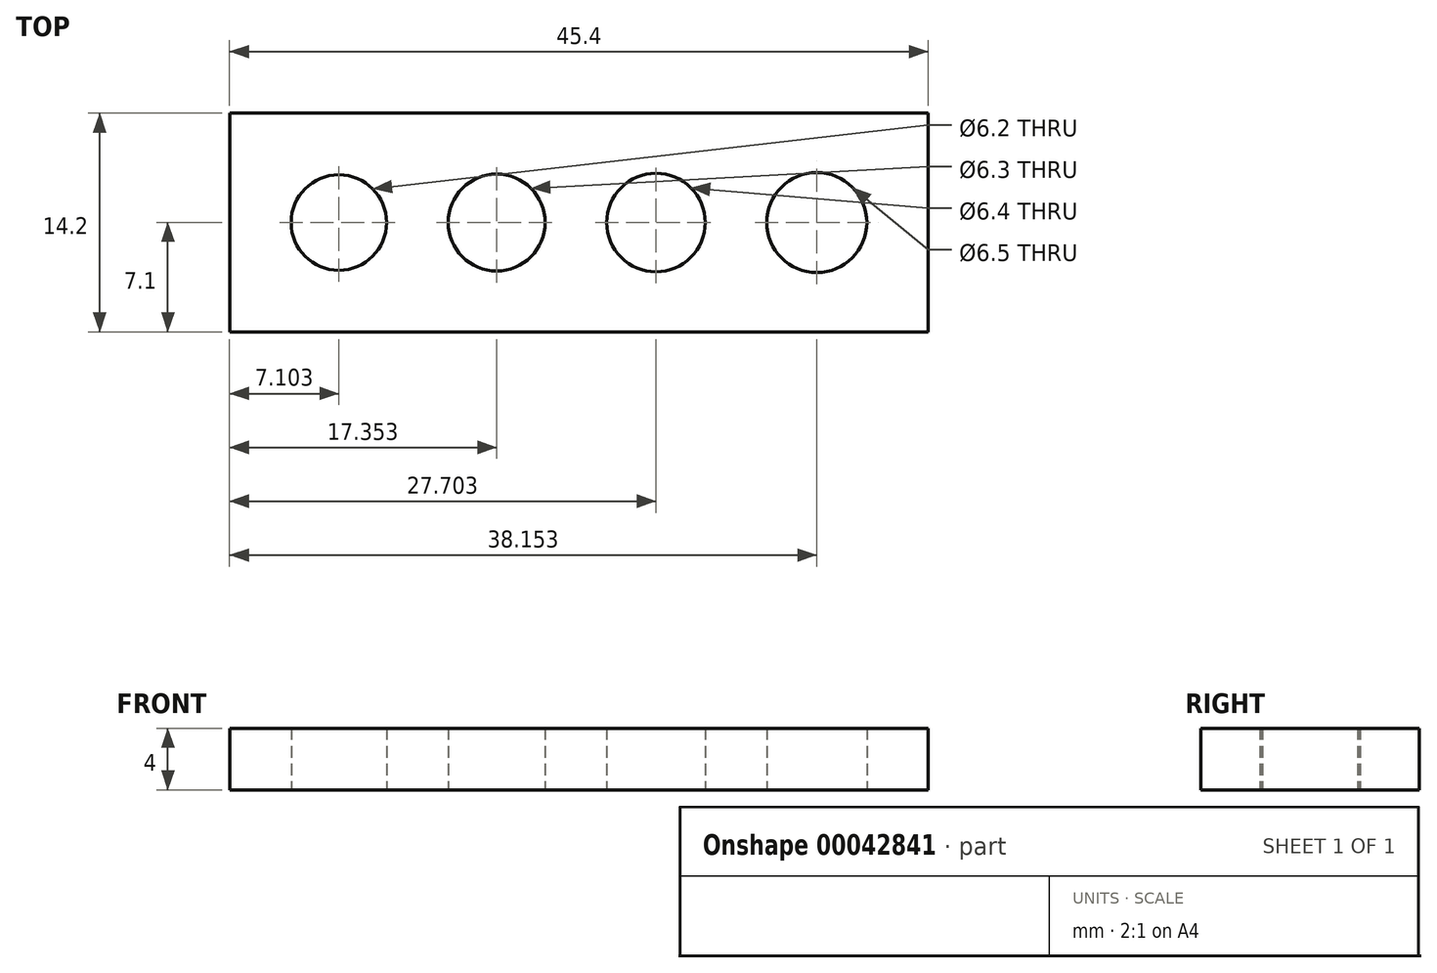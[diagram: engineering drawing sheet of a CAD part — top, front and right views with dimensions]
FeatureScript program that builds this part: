
annotation { "Feature Type Name" : "Feature", "Feature Type Description" : "" }
export const myFeature = defineFeature(function(context is Context, id is Id, definition is map)
    precondition{}
    {
        {
            var Q0;
            Q0=qCreatedBy(makeId("Top.planeOp"),FACE);
            var sketch = newSketch(context, id + "F0", { "sketchPlane" : qUnion([Q0])});
            skCircle(sketch, "E0", {"center": v(-16.23, 0) * mm, "radius": 3.1 * mm});
            skCircle(sketch, "E1", {"center": v(-5.98, 0) * mm, "radius": 3.15 * mm});
            skCircle(sketch, "E2", {"center": v(4.37, 0) * mm, "radius": 3.2 * mm});
            skCircle(sketch, "E3", {"center": v(14.82, 0) * mm, "radius": 3.25 * mm});
            skLineSegment(sketch, "E4.bottom", {"start": v(-23.33, 7.1) * mm, "end": v(22.07, 7.1) * mm});
            skLineSegment(sketch, "E4.top", {"start": v(-23.33, -7.1) * mm, "end": v(22.07, -7.1) * mm});
            skLineSegment(sketch, "E4.left", {"start": v(-23.33, 7.1) * mm, "end": v(-23.33, -7.1) * mm});
            skLineSegment(sketch, "E4.right", {"start": v(22.07, 7.1) * mm, "end": v(22.07, -7.1) * mm});
            skSolve(sketch);
        }
        {
            var Q0;
            Q0=makeQuery(id+"F0.imprint","IMPRINT",FACE,{"disambiguationData":[TD([[makeQuery(id+"F0.imprint","IMPRINT",EDGE,{"derivedFrom":sQuery(id+"F0.wireOp",EDGE,"E0")}),-1.0]])]});
            extrude(context, id + "F1", {"entities" : qUnion([Q0]), "depth" : 4 * mm});
        }
    });
